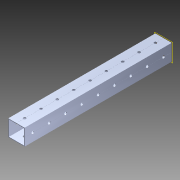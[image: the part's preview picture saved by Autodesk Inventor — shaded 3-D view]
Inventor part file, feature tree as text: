
AUTODESK INVENTOR PART (.ipt)
format: ipt  version: 2014 (Build 180170000, 170)  size: 1,154,048 bytes
history: native  units: in
note: dims shown in document units (in); Inventor stores cm internally (conversion verified against a paired STEP export)
features: pattern_circular x1, other x1, plane x1, extrude x1, imported_body x1, sketch x1
ambient origin geometry x8: Origin, YZ Plane, XZ Plane, XY Plane, X Axis, Y Axis, Z Axis, Center Point
bodies: Body1 (feature_tree)
feature tree (6):
  pattern_circular  "CirPattern2"
  other  "217-3426-STEP1"
  plane  "Work Plane1"
  extrude  "Extrusion1"  Depth=3937.0079in TaperAngle=0.0deg
  imported_body  "Base1"
  sketch  "Sketch1"  dims[d0=-9.0in d1=3937.0079in d2=0.0in]
